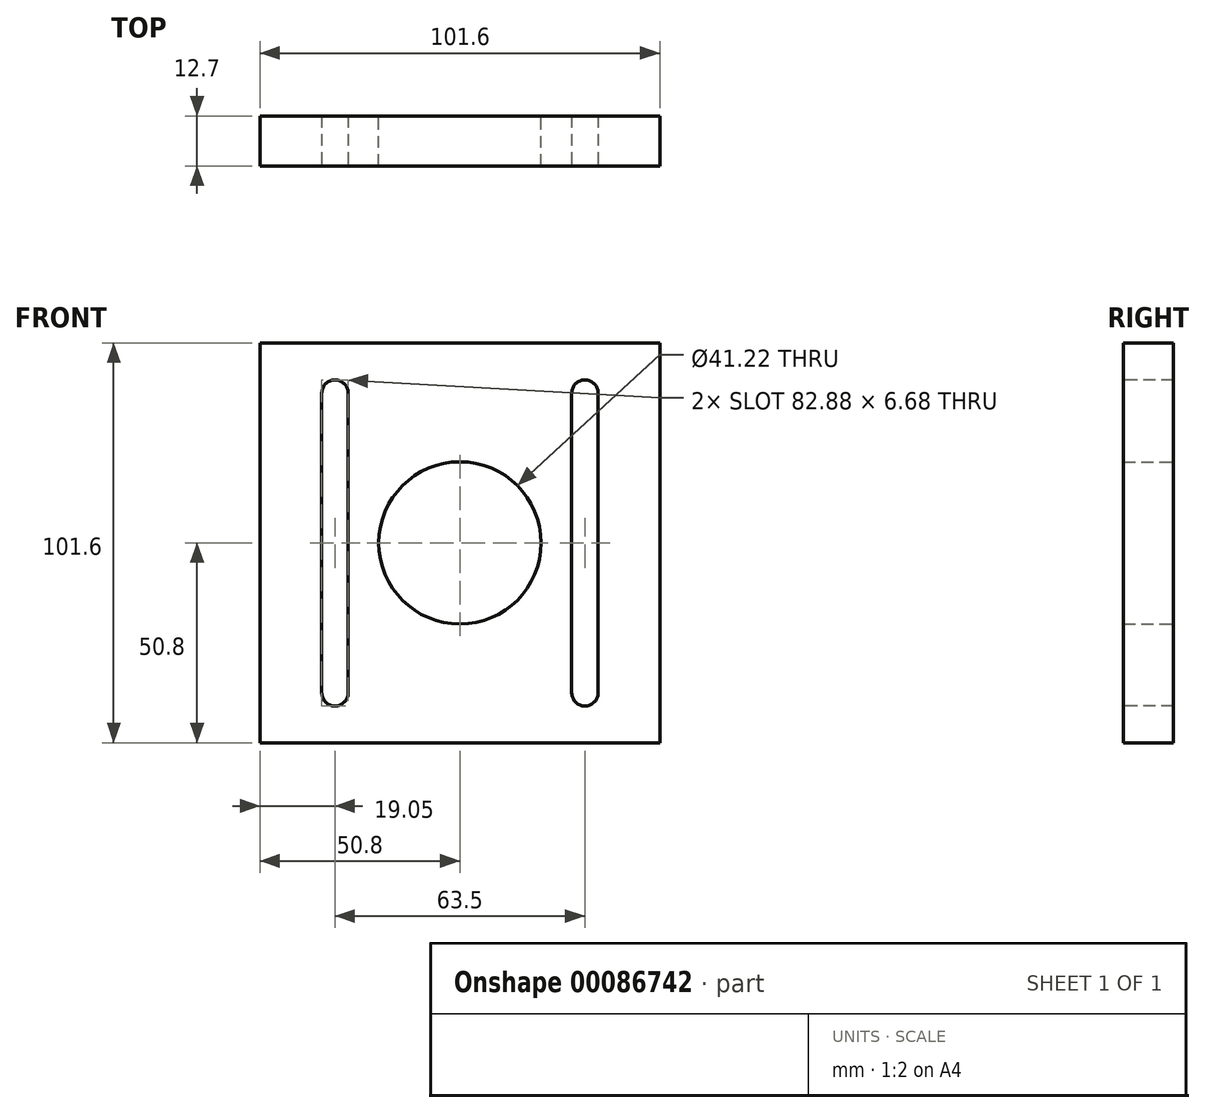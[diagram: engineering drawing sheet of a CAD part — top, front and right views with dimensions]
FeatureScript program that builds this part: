
annotation { "Feature Type Name" : "Feature", "Feature Type Description" : "" }
export const myFeature = defineFeature(function(context is Context, id is Id, definition is map)
    precondition{}
    {
        {
            var Q0;
            Q0=qCreatedBy(makeId("Front.planeOp"),FACE);
            var sketch = newSketch(context, id + "F0", { "sketchPlane" : qUnion([Q0])});
            skLineSegment(sketch, "E0.bottom", {"start": v(-50.8, 50.8) * mm, "end": v(50.8, 50.8) * mm});
            skLineSegment(sketch, "E0.top", {"start": v(-50.8, -50.8) * mm, "end": v(50.8, -50.8) * mm});
            skLineSegment(sketch, "E0.left", {"start": v(-50.8, 50.8) * mm, "end": v(-50.8, -50.8) * mm});
            skLineSegment(sketch, "E0.right", {"start": v(50.8, 50.8) * mm, "end": v(50.8, -50.8) * mm});
            skPoint(sketch, "E0.middle", {"position": v(0, 0) * mm});
            skCircle(sketch, "E1", {"center": v(0, 0) * mm, "radius": 20.61 * mm});
            skSolve(sketch);
        }
        {
            var Q0;
            Q0=makeQuery(id+"F0.imprint","IMPRINT",FACE,{"disambiguationData":[TD([[makeQuery(id+"F0.imprint","IMPRINT",EDGE,{"derivedFrom":sQuery(id+"F0.wireOp",EDGE,"E0.bottom")}),-1.0]])]});
            extrude(context, id + "F1", {"entities" : qUnion([Q0]), "depth" : 12.7 * mm});
        }
        {
            var Q0;
            Q0=makeQuery(id+"F1.opExtrude","CAP_FACE",FACE,{"disambiguationData":[OSD([sQuery(id+"F0.wireOp",EDGE,"E0.bottom"),sQuery(id+"F0.wireOp",EDGE,"E0.top"),sQuery(id+"F0.wireOp",EDGE,"E0.left"),sQuery(id+"F0.wireOp",EDGE,"E0.right"),sQuery(id+"F0.wireOp",EDGE,"E1")])],"isStart":false});
            var sketch = newSketch(context, id + "F2", { "sketchPlane" : qUnion([Q0])});
            skArc(sketch, "E2", {"start": v(-28.4, 38.1) * mm, "mid": v(-31.75, 41.44) * mm, "end": v(-35.1, 38.1) * mm});
            skArc(sketch, "E3", {"start": v(35.1, 38.1) * mm, "mid": v(31.75, 41.44) * mm, "end": v(28.4, 38.1) * mm});
            skArc(sketch, "E4", {"start": v(-35.1, -38.1) * mm, "mid": v(-31.75, -41.44) * mm, "end": v(-28.4, -38.1) * mm});
            skArc(sketch, "E5", {"start": v(28.4, -38.1) * mm, "mid": v(31.75, -41.44) * mm, "end": v(35.1, -38.1) * mm});
            skLineSegment(sketch, "E6", {"start": v(-35.1, 38.1) * mm, "end": v(-35.1, -38.1) * mm});
            skLineSegment(sketch, "E7", {"start": v(-28.4, 38.1) * mm, "end": v(-28.4, -38.1) * mm});
            skLineSegment(sketch, "E8", {"start": v(28.4, -38.1) * mm, "end": v(28.4, 38.1) * mm});
            skLineSegment(sketch, "E9", {"start": v(35.1, 38.1) * mm, "end": v(35.1, -38.1) * mm});
            skSolve(sketch);
        }
        {
            var Q0;
            Q0=makeQuery(id+"F2.imprint","IMPRINT",FACE,{"disambiguationData":[TD([[makeQuery(id+"F2.imprint","IMPRINT",EDGE,{"derivedFrom":sQuery(id+"F2.wireOp",EDGE,"E3")}),1.0]])]});
            var Q1;
            Q1=makeQuery(id+"F2.imprint","IMPRINT",FACE,{"disambiguationData":[TD([[makeQuery(id+"F2.imprint","IMPRINT",EDGE,{"derivedFrom":sQuery(id+"F2.wireOp",EDGE,"E2")}),1.0]])]});
            extrude(context, id + "F3", {"entities" : qUnion([Q0, Q1]), "operationType" : NewBodyOperationType.REMOVE, "endBound" : BoundingType.THROUGH_ALL, "oppositeDirection" : true, "depth" : 25.4 * mm});
        }
    });
